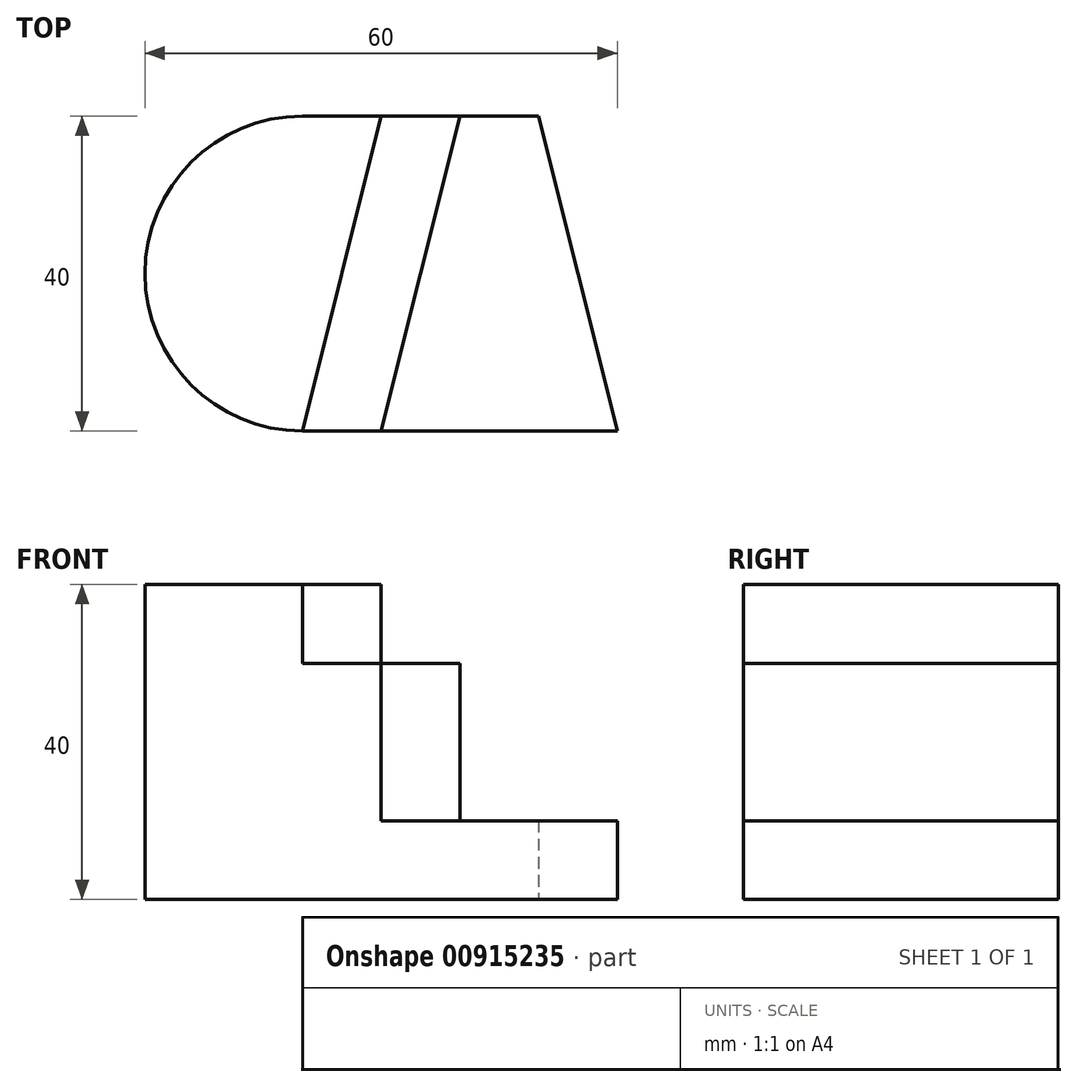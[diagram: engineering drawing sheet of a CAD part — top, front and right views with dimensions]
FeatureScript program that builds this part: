
annotation { "Feature Type Name" : "Feature", "Feature Type Description" : "" }
export const myFeature = defineFeature(function(context is Context, id is Id, definition is map)
    precondition{}
    {
        {
            var Q0;
            Q0=qCreatedBy(makeId("Top.planeOp"),FACE);
            var sketch = newSketch(context, id + "F0", { "sketchPlane" : qUnion([Q0])});
            skArc(sketch, "E0", {"start": v(0, 20) * mm, "mid": v(-20, 0) * mm, "end": v(0, -20) * mm});
            skLineSegment(sketch, "E1", {"start": v(0, 20) * mm, "end": v(30, 20) * mm});
            skLineSegment(sketch, "E2", {"start": v(30, 20) * mm, "end": v(40, -20) * mm});
            skLineSegment(sketch, "E3", {"start": v(40, -20) * mm, "end": v(0, -20) * mm});
            skLineSegment(sketch, "E4", {"start": v(10, -20) * mm, "end": v(20, 20) * mm});
            skLineSegment(sketch, "E5", {"start": v(0, -20) * mm, "end": v(10, 20) * mm});
            skSolve(sketch);
        }
        {
            var Q0;
            {var subQ0=sQuery(id+"F0.wireOp",EDGE,"E0");Q0=makeQuery(id+"F0.imprint","IMPRINT",FACE,{"disambiguationData":[TD([[makeQuery(id+"F0.imprint","IMPRINT",EDGE,{"derivedFrom":subQ0}),1.0]])]});}
            extrude(context, id + "F1", {"entities" : qUnion([Q0]), "depth" : 40 * mm, "offsetDistance" : 25 * mm});
        }
        {
            var Q0;
            {var subQ0=sQuery(id+"F0.wireOp",EDGE,"E4");Q0=makeQuery(id+"F0.imprint","IMPRINT",FACE,{"disambiguationData":[TD([[makeQuery(id+"F0.imprint","IMPRINT",EDGE,{"derivedFrom":subQ0}),1.0]])]});}
            extrude(context, id + "F2", {"entities" : qUnion([Q0]), "operationType" : NewBodyOperationType.ADD, "depth" : 30 * mm, "offsetDistance" : 25 * mm});
        }
        {
            var Q0;
            {var subQ0=sQuery(id+"F0.wireOp",EDGE,"E2");Q0=makeQuery(id+"F0.imprint","IMPRINT",FACE,{"disambiguationData":[TD([[makeQuery(id+"F0.imprint","IMPRINT",EDGE,{"derivedFrom":subQ0}),-1.0]])]});}
            extrude(context, id + "F3", {"entities" : qUnion([Q0]), "operationType" : NewBodyOperationType.ADD, "depth" : 10 * mm, "offsetDistance" : 25 * mm});
        }
    });
